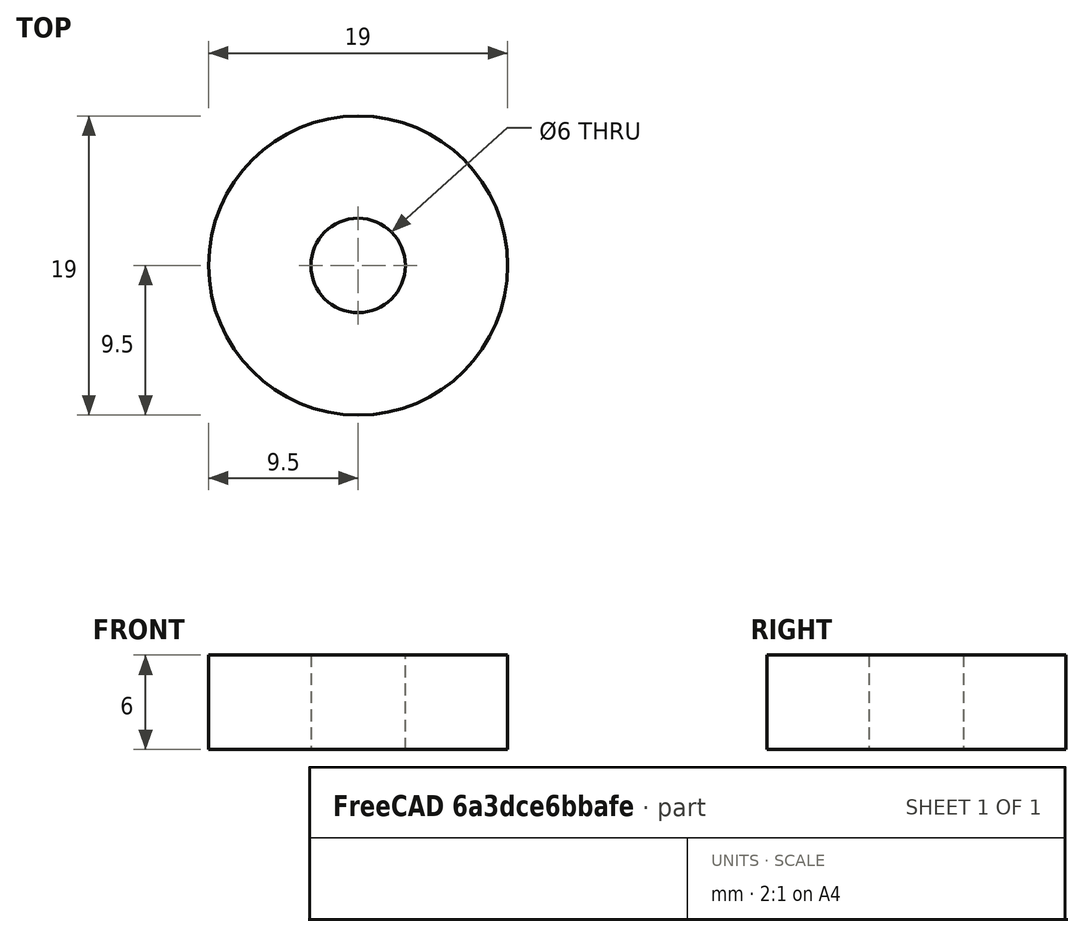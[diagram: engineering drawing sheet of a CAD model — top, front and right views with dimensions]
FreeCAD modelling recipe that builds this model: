
FCSTD DOCUMENT  (FreeCAD 0.19R24276 (Git))
Label: BALL-6-19-6
License: All rights reserved
LicenseURL: http://en.wikipedia.org/wiki/All_rights_reserved
objects: PartDesign::CoordinateSystem×3, Sketcher::SketchObject×1, PartDesign::Pad×1, PartDesign::Body×1, App::Part×1
note: 7 computed .brp shape members not serialized (recipe doc carries the construction recipe); baked Part::Feature solids carry a one-line shape summary decoded from their .brp

FEATURE [PartDesign::CoordinateSystem] LCS_0
  AttacherType = Attacher::AttachEngine3D
  MapMode = 2
  Support = -> [X_Axis]
FEATURE [PartDesign::CoordinateSystem] LCS_0001
  AttacherType = Attacher::AttachEngine3D
  MapMode = 2
  Support = -> [X_Axis001]
FEATURE [Sketcher::SketchObject] Sketch
  FullyConstrained = false
  MapMode = 5
  Support = -> [XY_Plane001]
  sketch-geometry (2):
    g0: Circle CenterX=0 CenterY=0 CenterZ=0 NormalX=0 NormalY=0 NormalZ=1 AngleXU=0 Radius=3
    g1: Circle CenterX=0 CenterY=0 CenterZ=0 NormalX=0 NormalY=0 NormalZ=1 AngleXU=0 Radius=9.5
  constraints (4):
    c: Coincident(g0,g-1)
    c: Coincident(g1,g0)
    c: Diameter(g0) = 6
    c: Diameter(g1) = 19
FEATURE [PartDesign::Pad] Pad
  Direction = (1,1,1)
  Length = 6
  Length2 = 100
  Profile = -> Sketch
  Refine = true
  Type = 0
FEATURE [PartDesign::Body] Body
  Group = -> [LCS_0001,Sketch,Pad]
  Origin = -> Origin001
  Tip = -> Pad
FEATURE [PartDesign::CoordinateSystem] LCS_1
  AttacherType = Attacher::AttachEngine3D
  MapMode = 11
  Placement = pos=(0,0,6) rot=(0,0,1;1.5708rad)
  Support = -> [Pad]
FEATURE [App::Part] Part
  Group = -> [LCS_0,Body,LCS_1]
  Origin = -> Origin
